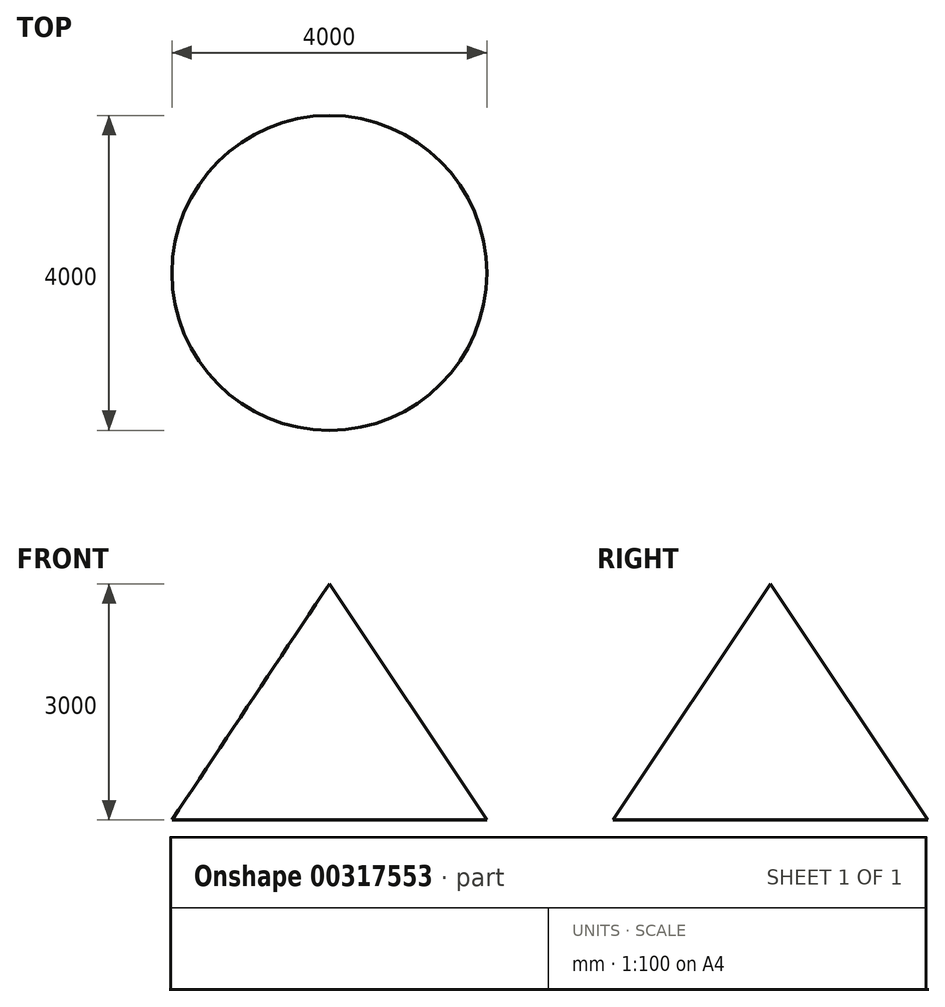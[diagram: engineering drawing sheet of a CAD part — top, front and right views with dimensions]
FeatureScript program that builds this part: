
annotation { "Feature Type Name" : "Feature", "Feature Type Description" : "" }
export const myFeature = defineFeature(function(context is Context, id is Id, definition is map)
    precondition{}
    {
        {
            var Q0;
            Q0=qCreatedBy(makeId("Front.planeOp"),FACE);
            var sketch = newSketch(context, id + "F0", { "sketchPlane" : qUnion([Q0])});
            skLineSegment(sketch, "E0", {"start": v(0, -1560.6) * mm, "end": v(0, 1439.4) * mm});
            skLineSegment(sketch, "E1", {"start": v(0, 1602.53) * mm, "end": v(0, -1842.13) * mm, "construction": true});
            skLineSegment(sketch, "E2", {"start": v(0, -1560.6) * mm, "end": v(2000, -1560.6) * mm});
            skLineSegment(sketch, "E3", {"start": v(2000, -1560.6) * mm, "end": v(0, 1439.4) * mm});
            skSolve(sketch);
        }
        {
            var Q0;
            Q0=makeQuery(id+"F0.imprint","IMPRINT",FACE,{"disambiguationData":[TD([[makeQuery(id+"F0.imprint","IMPRINT",EDGE,{"derivedFrom":sQuery(id+"F0.wireOp",EDGE,"E0")}),-1.0]])]});
            var Q1;
            Q1=sQuery(id+"F0.wireOp",EDGE,"E1");
            revolve(context, id + "F1", {"entities" : qUnion([Q0]), "axis" : qUnion([Q1]), "revolveType" : RevolveType.FULL});
        }
    });
